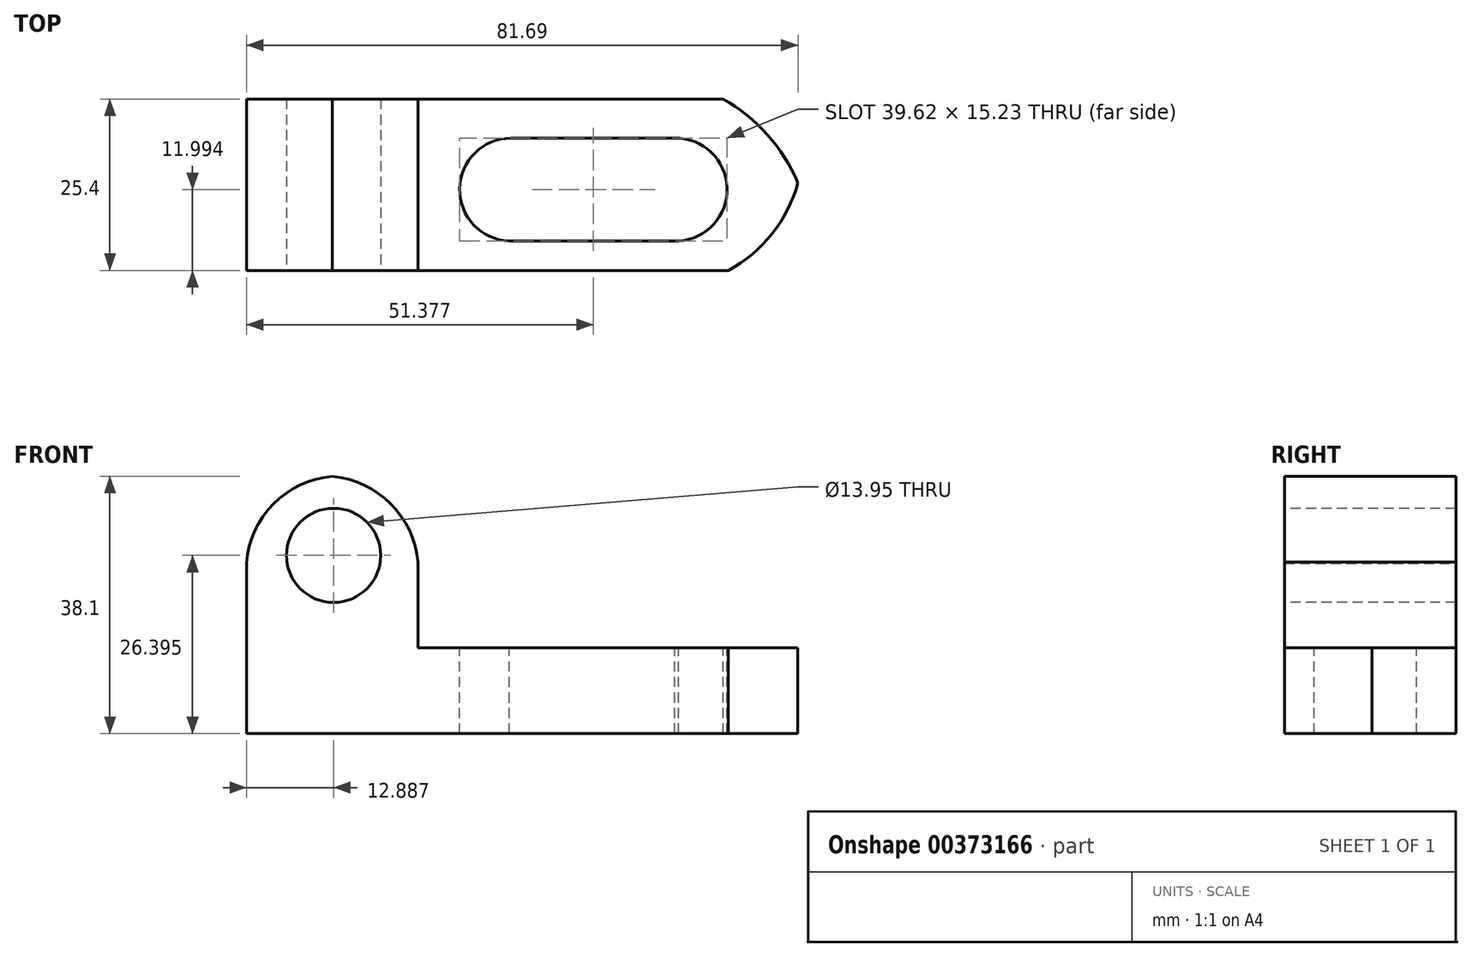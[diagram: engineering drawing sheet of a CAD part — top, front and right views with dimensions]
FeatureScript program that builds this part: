
annotation { "Feature Type Name" : "Feature", "Feature Type Description" : "" }
export const myFeature = defineFeature(function(context is Context, id is Id, definition is map)
    precondition{}
    {
        {
            var Q0;
            Q0=qCreatedBy(makeId("Front.planeOp"),FACE);
            var sketch = newSketch(context, id + "F0", { "sketchPlane" : qUnion([Q0])});
            skLineSegment(sketch, "E0", {"start": v(0, 0) * mm, "end": v(0, 38.1) * mm});
            skLineSegment(sketch, "E1", {"start": v(0, 38.1) * mm, "end": v(25.4, 38.1) * mm});
            skLineSegment(sketch, "E2", {"start": v(25.4, 38.1) * mm, "end": v(25.4, 12.7) * mm});
            skLineSegment(sketch, "E3", {"start": v(25.4, 12.7) * mm, "end": v(82.55, 12.7) * mm});
            skLineSegment(sketch, "E4", {"start": v(82.55, 12.7) * mm, "end": v(82.55, 0) * mm});
            skLineSegment(sketch, "E5", {"start": v(82.55, 0) * mm, "end": v(0, 0) * mm});
            skArc(sketch, "E6", {"start": v(12.7, 38.1) * mm, "mid": v(3.98, 34.02) * mm, "end": v(0, 25.24) * mm});
            skArc(sketch, "E7", {"start": v(25.4, 25.4) * mm, "mid": v(21.34, 34.04) * mm, "end": v(12.7, 38.1) * mm});
            skSolve(sketch);
        }
        {
            var Q0;
            {var subQ0=sQuery(id+"F0.wireOp",EDGE,"E3");Q0=makeQuery(id+"F0.imprint","IMPRINT",FACE,{"disambiguationData":[TD([[makeQuery(id+"F0.imprint","IMPRINT",EDGE,{"derivedFrom":subQ0}),-1.0]])]});}
            extrude(context, id + "F1", {"entities" : qUnion([Q0]), "depth" : 25.4 * mm});
        }
        {
            var Q0;
            Q0=makeQuery(id+"F1.opExtrude","SWEPT_FACE",FACE,{"disambiguationData":[OSD([sQuery(id+"F0.wireOp",EDGE,"E3")])]});
            var sketch = newSketch(context, id + "F2", { "sketchPlane" : qUnion([Q0])});
            skArc(sketch, "E8", {"start": v(82.55, -12.7) * mm, "mid": v(78.11, -4.9) * mm, "end": v(70.6, 0) * mm});
            skArc(sketch, "E9", {"start": v(71.38, -25.4) * mm, "mid": v(78.61, -20.5) * mm, "end": v(82.55, -12.7) * mm});
            skSolve(sketch);
        }
        {
            var Q0;
            {var subQ0=sQuery(id+"F2.wireOp",EDGE,"E8");Q0=makeQuery(id+"F2.imprint","IMPRINT",FACE,{"disambiguationData":[TD([[makeQuery(id+"F2.imprint","IMPRINT",EDGE,{"derivedFrom":subQ0}),-1.0]])]});}
            var Q1;
            {var subQ0=sQuery(id+"F2.wireOp",EDGE,"E9");Q1=makeQuery(id+"F2.imprint","IMPRINT",FACE,{"disambiguationData":[TD([[makeQuery(id+"F2.imprint","IMPRINT",EDGE,{"derivedFrom":subQ0}),-1.0]])]});}
            extrude(context, id + "F3", {"entities" : qUnion([Q0, Q1]), "operationType" : NewBodyOperationType.REMOVE, "oppositeDirection" : true, "depth" : 25.4 * mm});
        }
        {
            var Q0;
            Q0=makeQuery(id+"F1.opExtrude","CAP_FACE",FACE,{"disambiguationData":[OSD([sQuery(id+"F0.wireOp",EDGE,"E0"),sQuery(id+"F0.wireOp",EDGE,"E2"),sQuery(id+"F0.wireOp",EDGE,"E3"),sQuery(id+"F0.wireOp",EDGE,"E4"),sQuery(id+"F0.wireOp",EDGE,"E5"),sQuery(id+"F0.wireOp",EDGE,"E6"),sQuery(id+"F0.wireOp",EDGE,"E7")])],"isStart":false});
            var sketch = newSketch(context, id + "F4", { "sketchPlane" : qUnion([Q0])});
            skCircle(sketch, "E10", {"center": v(12.89, 26.4) * mm, "radius": 6.98 * mm});
            skSolve(sketch);
        }
        {
            var Q0;
            Q0=makeQuery(id+"F4.imprint","IMPRINT",FACE,{"disambiguationData":[TD([[makeQuery(id+"F4.imprint","IMPRINT",EDGE,{"derivedFrom":sQuery(id+"F4.wireOp",EDGE,"E10")}),1.0]])]});
            extrude(context, id + "F5", {"entities" : qUnion([Q0]), "operationType" : NewBodyOperationType.REMOVE, "oppositeDirection" : true, "depth" : 25.4 * mm});
        }
        {
            var Q0;
            Q0=makeQuery(id+"F1.opExtrude","SWEPT_FACE",FACE,{"disambiguationData":[OSD([sQuery(id+"F0.wireOp",EDGE,"E3")])]});
            var sketch = newSketch(context, id + "F6", { "sketchPlane" : qUnion([Q0])});
            skCircle(sketch, "E11", {"center": v(63.57, -13.41) * mm, "radius": 7.62 * mm});
            skCircle(sketch, "E12", {"center": v(39.18, -13.41) * mm, "radius": 7.61 * mm});
            skLineSegment(sketch, "E13", {"start": v(63.45, -5.8) * mm, "end": v(39.18, -5.8) * mm});
            skLineSegment(sketch, "E14", {"start": v(38.94, -21.02) * mm, "end": v(63.99, -21.02) * mm});
            skSolve(sketch);
        }
        {
            var Q0;
            {var subQ0=sQuery(id+"F6.wireOp",EDGE,"E12");var subQ1=makeQuery(id+"F6.imprint","INTERSECT",VERTEX,{"derivedFrom":[subQ0,sQuery(id+"F6.wireOp",EDGE,"E13")]});Q0=makeQuery(id+"F6.imprint","IMPRINT",FACE,{"disambiguationData":[TD([[makeQuery(id+"F6.imprint","IMPRINT",EDGE,{"disambiguationData":[TD([[subQ1,-1.0]])],"derivedFrom":subQ0}),1.0]])]});}
            var Q1;
            {var subQ0=sQuery(id+"F6.wireOp",EDGE,"E13");Q1=makeQuery(id+"F6.imprint","IMPRINT",FACE,{"disambiguationData":[TD([[makeQuery(id+"F6.imprint","IMPRINT",EDGE,{"derivedFrom":subQ0}),1.0]])]});}
            var Q2;
            {var subQ0=sQuery(id+"F6.wireOp",EDGE,"E11");var subQ1=makeQuery(id+"F6.imprint","INTERSECT",VERTEX,{"derivedFrom":[subQ0,sQuery(id+"F6.wireOp",EDGE,"E13")]});Q2=makeQuery(id+"F6.imprint","IMPRINT",FACE,{"disambiguationData":[TD([[makeQuery(id+"F6.imprint","IMPRINT",EDGE,{"disambiguationData":[TD([[subQ1,-1.0]])],"derivedFrom":subQ0}),1.0]])]});}
            extrude(context, id + "F7", {"entities" : qUnion([Q0, Q1, Q2]), "operationType" : NewBodyOperationType.REMOVE, "oppositeDirection" : true, "depth" : 25.4 * mm});
        }
        {
            var Q0;
            Q0=makeQuery(id+"F1.opExtrude","SWEPT_FACE",FACE,{"disambiguationData":[OSD([sQuery(id+"F0.wireOp",EDGE,"E3")])]});
            var sketch = newSketch(context, id + "F8", { "sketchPlane" : qUnion([Q0])});
            skArc(sketch, "E15", {"start": v(81.69, -12.42) * mm, "mid": v(77.18, -5.29) * mm, "end": v(70.6, 0) * mm});
            skArc(sketch, "E16", {"start": v(71.38, -25.4) * mm, "mid": v(77.86, -19.96) * mm, "end": v(81.69, -12.42) * mm});
            skSolve(sketch);
        }
        {
            var Q0;
            Q0 = qSketchRegion(id + "F8", true);
            var Q1;
            Q1=makeQuery(id+"F8.imprint","IMPRINT",FACE,{"disambiguationData":[TD([[makeQuery(id+"F8.imprint","IMPRINT",EDGE,{"derivedFrom":sQuery(id+"F8.wireOp",EDGE,"E15")}),-1.0]])]});
            extrude(context, id + "F9", {"entities" : qUnion([Q0, Q1]), "operationType" : NewBodyOperationType.REMOVE, "oppositeDirection" : true, "depth" : 25.4 * mm});
        }
    });
